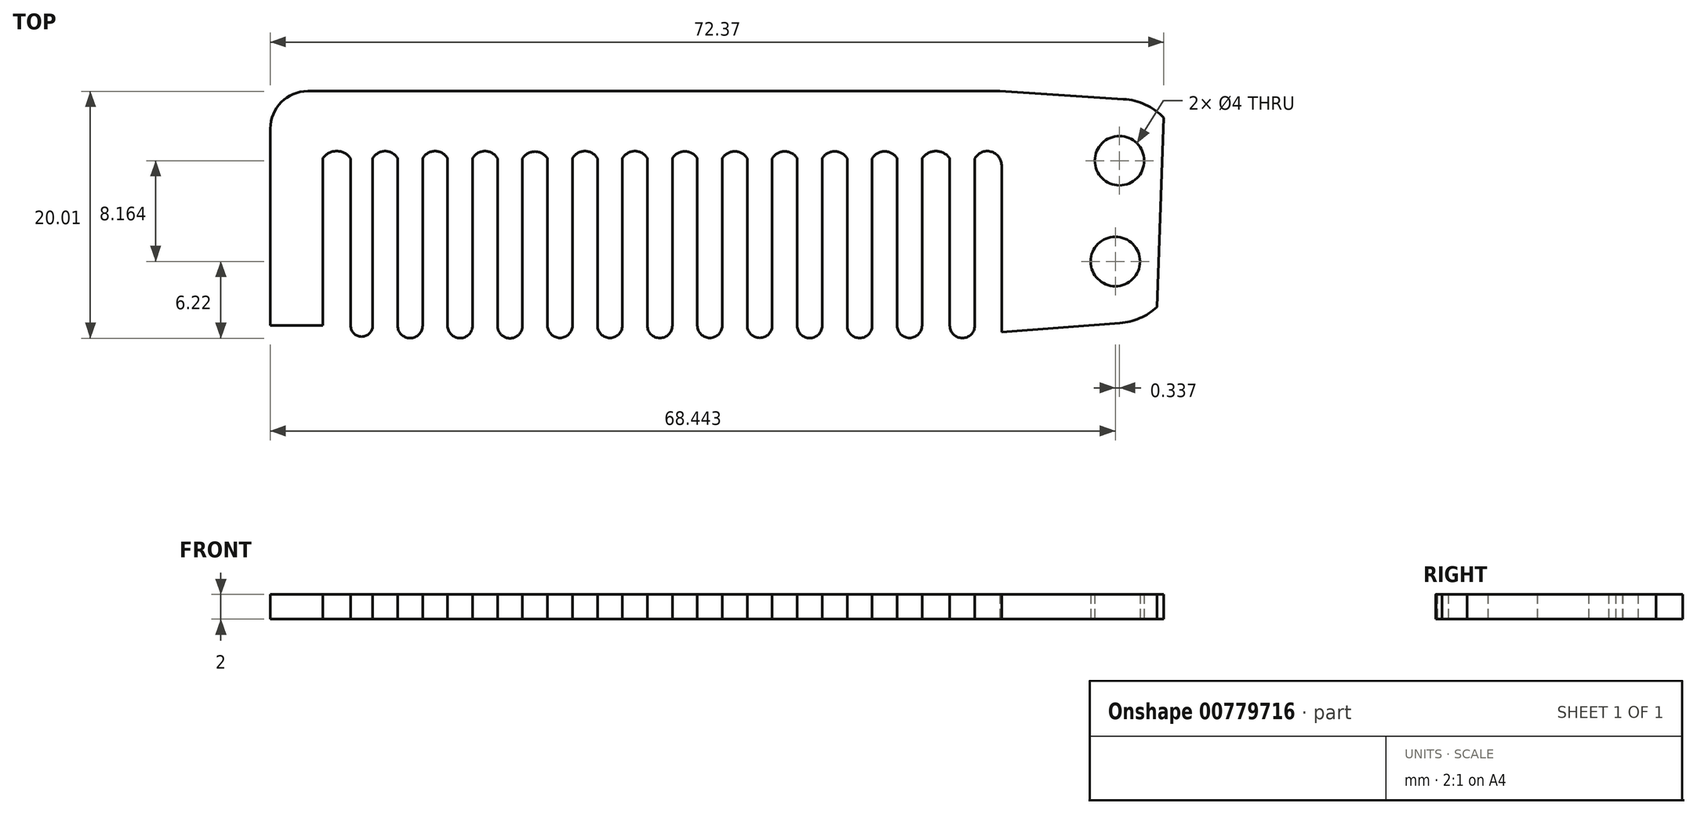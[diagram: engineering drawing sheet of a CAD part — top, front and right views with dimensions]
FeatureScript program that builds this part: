
annotation { "Feature Type Name" : "Feature", "Feature Type Description" : "" }
export const myFeature = defineFeature(function(context is Context, id is Id, definition is map)
    precondition{}
    {
        {
            var Q0;
            Q0=qCreatedBy(makeId("Top.planeOp"),FACE);
            var sketch = newSketch(context, id + "F0", { "sketchPlane" : qUnion([Q0])});
            skLineSegment(sketch, "E0", {"start": v(56.63, 10.5) * mm, "end": v(56.63, -3.03) * mm});
            skArc(sketch, "E1.filletArc", {"start": v(2.6, 15.95) * mm, "mid": v(0.46, 15.07) * mm, "end": v(-0.43, 12.92) * mm});
            skLineSegment(sketch, "E2", {"start": v(3.82, 2.37) * mm, "end": v(3.82, -3.03) * mm});
            skLineSegment(sketch, "E3", {"start": v(3.82, -3.03) * mm, "end": v(3.82, 10.5) * mm});
            skLineSegment(sketch, "E4", {"start": v(6.08, 2.37) * mm, "end": v(6.08, 10.5) * mm});
            skLineSegment(sketch, "E5", {"start": v(6.08, 10.5) * mm, "end": v(6.08, -3.03) * mm});
            skLineSegment(sketch, "E6", {"start": v(7.86, 2.37) * mm, "end": v(7.86, 10.5) * mm});
            skLineSegment(sketch, "E7", {"start": v(7.86, 10.5) * mm, "end": v(7.86, -3.03) * mm});
            skLineSegment(sketch, "E8", {"start": v(9.89, 2.37) * mm, "end": v(9.89, 10.5) * mm});
            skLineSegment(sketch, "E9", {"start": v(9.89, 10.5) * mm, "end": v(9.89, -3.03) * mm});
            skLineSegment(sketch, "E10", {"start": v(11.9, 2.37) * mm, "end": v(11.9, 10.5) * mm});
            skLineSegment(sketch, "E11", {"start": v(11.9, 10.5) * mm, "end": v(11.9, -3.03) * mm});
            skLineSegment(sketch, "E12", {"start": v(13.93, 2.37) * mm, "end": v(13.93, 10.5) * mm});
            skLineSegment(sketch, "E13", {"start": v(13.93, 10.5) * mm, "end": v(13.93, -3.03) * mm});
            skLineSegment(sketch, "E14", {"start": v(15.95, 2.37) * mm, "end": v(15.95, 10.5) * mm});
            skLineSegment(sketch, "E15", {"start": v(15.95, 10.5) * mm, "end": v(15.95, -3.03) * mm});
            skLineSegment(sketch, "E16", {"start": v(17.98, 10.5) * mm, "end": v(17.98, -3.06) * mm});
            skLineSegment(sketch, "E17", {"start": v(20, 2.37) * mm, "end": v(20, 10.5) * mm});
            skLineSegment(sketch, "E18", {"start": v(20, 10.5) * mm, "end": v(20, -3.06) * mm});
            skLineSegment(sketch, "E19", {"start": v(22.02, 2.37) * mm, "end": v(22.02, 10.5) * mm});
            skLineSegment(sketch, "E20", {"start": v(24.04, 2.37) * mm, "end": v(24.04, 10.5) * mm});
            skLineSegment(sketch, "E21", {"start": v(24.04, 2.37) * mm, "end": v(24.04, -3.03) * mm});
            skLineSegment(sketch, "E22", {"start": v(26.07, 2.37) * mm, "end": v(26.07, 10.5) * mm});
            skLineSegment(sketch, "E23", {"start": v(26.07, 10.5) * mm, "end": v(26.07, -3.03) * mm});
            skLineSegment(sketch, "E24", {"start": v(28.09, 2.37) * mm, "end": v(28.09, 10.5) * mm});
            skLineSegment(sketch, "E25", {"start": v(28.09, 2.37) * mm, "end": v(28.09, -3.03) * mm});
            skLineSegment(sketch, "E26", {"start": v(30.11, 2.37) * mm, "end": v(30.11, 10.5) * mm});
            skLineSegment(sketch, "E27", {"start": v(30.11, 10.5) * mm, "end": v(30.11, -3.03) * mm});
            skLineSegment(sketch, "E28", {"start": v(32.13, 2.37) * mm, "end": v(32.13, 10.5) * mm});
            skLineSegment(sketch, "E29", {"start": v(32.13, 10.5) * mm, "end": v(32.13, -3.03) * mm});
            skLineSegment(sketch, "E30", {"start": v(34.16, 2.37) * mm, "end": v(34.16, 10.5) * mm});
            skLineSegment(sketch, "E31", {"start": v(34.16, 10.5) * mm, "end": v(34.16, -3.03) * mm});
            skLineSegment(sketch, "E32", {"start": v(36.18, 2.37) * mm, "end": v(36.18, 10.5) * mm});
            skLineSegment(sketch, "E33", {"start": v(36.18, 10.5) * mm, "end": v(36.18, -3.03) * mm});
            skLineSegment(sketch, "E34", {"start": v(38.2, 2.37) * mm, "end": v(38.2, 10.5) * mm});
            skLineSegment(sketch, "E35", {"start": v(38.2, 10.5) * mm, "end": v(38.2, -3.03) * mm});
            skLineSegment(sketch, "E36", {"start": v(40.23, 2.37) * mm, "end": v(40.23, 10.5) * mm});
            skLineSegment(sketch, "E37", {"start": v(40.23, 10.5) * mm, "end": v(40.23, -3.03) * mm});
            skLineSegment(sketch, "E38", {"start": v(42.25, 2.37) * mm, "end": v(42.25, 10.5) * mm});
            skLineSegment(sketch, "E39", {"start": v(42.25, 10.5) * mm, "end": v(42.25, -3.03) * mm});
            skLineSegment(sketch, "E40", {"start": v(44.27, 2.37) * mm, "end": v(44.27, 10.5) * mm});
            skLineSegment(sketch, "E41", {"start": v(44.27, 10.5) * mm, "end": v(44.27, -3.03) * mm});
            skLineSegment(sketch, "E42", {"start": v(46.3, 2.37) * mm, "end": v(46.3, 10.5) * mm});
            skLineSegment(sketch, "E43", {"start": v(46.3, 10.5) * mm, "end": v(46.3, -3.03) * mm});
            skLineSegment(sketch, "E44", {"start": v(48.32, 2.37) * mm, "end": v(48.32, 10.5) * mm});
            skLineSegment(sketch, "E45", {"start": v(48.32, 10.5) * mm, "end": v(48.32, -3.03) * mm});
            skLineSegment(sketch, "E46", {"start": v(50.34, 2.37) * mm, "end": v(50.34, 10.5) * mm});
            skLineSegment(sketch, "E47", {"start": v(50.34, 10.5) * mm, "end": v(50.34, -3.03) * mm});
            skLineSegment(sketch, "E48", {"start": v(52.36, 2.37) * mm, "end": v(52.36, 10.5) * mm});
            skLineSegment(sketch, "E49", {"start": v(52.36, 10.5) * mm, "end": v(52.36, -3.03) * mm});
            skLineSegment(sketch, "E50", {"start": v(54.6, 2.37) * mm, "end": v(54.6, 10.5) * mm});
            skLineSegment(sketch, "E51", {"start": v(54.6, 10.5) * mm, "end": v(54.6, -3.03) * mm});
            skLineSegment(sketch, "E52", {"start": v(58.8, 9.96) * mm, "end": v(58.8, -3.3) * mm});
            skArc(sketch, "E53", {"start": v(9.89, -3.03) * mm, "mid": v(10.9, -4.05) * mm, "end": v(11.9, -3.03) * mm});
            skArc(sketch, "E54", {"start": v(13.93, -3.03) * mm, "mid": v(14.94, -4.05) * mm, "end": v(15.95, -3.03) * mm});
            skArc(sketch, "E55", {"start": v(17.98, -3.03) * mm, "mid": v(18.99, -4.06) * mm, "end": v(20, -3.03) * mm});
            skArc(sketch, "E56", {"start": v(22.02, -3.03) * mm, "mid": v(23.03, -4.03) * mm, "end": v(24.04, -3.03) * mm});
            skArc(sketch, "E57", {"start": v(26.07, -3.03) * mm, "mid": v(27.08, -4.03) * mm, "end": v(28.09, -3.03) * mm});
            skArc(sketch, "E58", {"start": v(30.11, -3.03) * mm, "mid": v(31.12, -4.04) * mm, "end": v(32.13, -3.03) * mm});
            skArc(sketch, "E59", {"start": v(34.16, -3.03) * mm, "mid": v(35.17, -4.03) * mm, "end": v(36.18, -3.03) * mm});
            skArc(sketch, "E60", {"start": v(38.2, -3.03) * mm, "mid": v(39.21, -4.02) * mm, "end": v(40.23, -3.03) * mm});
            skArc(sketch, "E61", {"start": v(42.25, -3.03) * mm, "mid": v(43.26, -4.05) * mm, "end": v(44.27, -3.03) * mm});
            skArc(sketch, "E62", {"start": v(46.3, -3.03) * mm, "mid": v(47.3, -4.04) * mm, "end": v(48.32, -3.03) * mm});
            skArc(sketch, "E63", {"start": v(50.34, -3.03) * mm, "mid": v(51.35, -4.03) * mm, "end": v(52.36, -3.03) * mm});
            skArc(sketch, "E64", {"start": v(54.6, -3.03) * mm, "mid": v(55.62, -4.04) * mm, "end": v(56.63, -3.03) * mm});
            skArc(sketch, "E65.filletArc", {"start": v(58.8, -3.3) * mm, "mid": v(58.8, -3.43) * mm, "end": v(58.81, -3.55) * mm});
            skArc(sketch, "E66", {"start": v(6.08, -3.03) * mm, "mid": v(6.97, -3.93) * mm, "end": v(7.86, -3.03) * mm});
            skArc(sketch, "E67", {"start": v(6.08, 10.5) * mm, "mid": v(4.95, 11.1) * mm, "end": v(3.82, 10.5) * mm});
            skArc(sketch, "E68", {"start": v(9.89, 10.5) * mm, "mid": v(8.87, 11.1) * mm, "end": v(7.86, 10.5) * mm});
            skArc(sketch, "E69", {"start": v(13.93, 10.5) * mm, "mid": v(12.92, 11.1) * mm, "end": v(11.9, 10.5) * mm});
            skArc(sketch, "E70", {"start": v(17.98, 10.5) * mm, "mid": v(16.97, 11.1) * mm, "end": v(15.95, 10.5) * mm});
            skArc(sketch, "E71", {"start": v(22.02, 10.5) * mm, "mid": v(21.01, 11.06) * mm, "end": v(20, 10.5) * mm});
            skArc(sketch, "E72", {"start": v(26.07, 10.5) * mm, "mid": v(25.06, 11.1) * mm, "end": v(24.04, 10.5) * mm});
            skArc(sketch, "E73", {"start": v(30.11, 10.5) * mm, "mid": v(29.1, 11.1) * mm, "end": v(28.09, 10.5) * mm});
            skArc(sketch, "E74", {"start": v(34.16, 10.5) * mm, "mid": v(33.15, 11.08) * mm, "end": v(32.13, 10.5) * mm});
            skArc(sketch, "E75", {"start": v(38.2, 10.5) * mm, "mid": v(37.2, 11.08) * mm, "end": v(36.18, 10.5) * mm});
            skArc(sketch, "E76", {"start": v(42.25, 10.5) * mm, "mid": v(41.24, 11.08) * mm, "end": v(40.23, 10.5) * mm});
            skArc(sketch, "E77", {"start": v(46.3, 10.5) * mm, "mid": v(45.28, 11.08) * mm, "end": v(44.27, 10.5) * mm});
            skArc(sketch, "E78", {"start": v(50.34, 10.5) * mm, "mid": v(49.33, 11.08) * mm, "end": v(48.32, 10.5) * mm});
            skArc(sketch, "E79", {"start": v(54.6, 10.5) * mm, "mid": v(53.49, 11.1) * mm, "end": v(52.36, 10.5) * mm});
            skArc(sketch, "E80", {"start": v(58.8, 9.96) * mm, "mid": v(57.93, 11.06) * mm, "end": v(56.63, 10.5) * mm});
            skLineSegment(sketch, "E81", {"start": v(22.02, 2.37) * mm, "end": v(22.02, -3.03) * mm});
            skLineSegment(sketch, "E82", {"start": v(78.8, 5.95) * mm, "end": v(78.8, 5.95) * mm});
            skLineSegment(sketch, "E83", {"start": v(2.6, 15.95) * mm, "end": v(58.65, 15.95) * mm});
            skPoint(sketch, "E84.visualSharp", {"position": v(78.8, -4.05) * mm});
            skPoint(sketch, "E85.visualSharp", {"position": v(78.8, 15.95) * mm});
            skPoint(sketch, "E86.visualSharp", {"position": v(78.8, 5.95) * mm});
            skCircle(sketch, "E87", {"center": v(68.01, 2.16) * mm, "radius": 2 * mm});
            skCircle(sketch, "E88", {"center": v(68.35, 10.32) * mm, "radius": 2 * mm});
            skLineSegment(sketch, "E89", {"start": v(58.65, 15.95) * mm, "end": v(68.67, 15.31) * mm});
            skLineSegment(sketch, "E90", {"start": v(58.81, -3.55) * mm, "end": v(68.4, -2.83) * mm});
            skPoint(sketch, "E91.visualSharp", {"position": v(70.4, 15.2) * mm});
            skArc(sketch, "E91.filletArc", {"start": v(71.94, 13.8) * mm, "mid": v(70.45, 14.86) * mm, "end": v(68.67, 15.31) * mm});
            skPoint(sketch, "E92.visualSharp", {"position": v(70.33, -2.68) * mm});
            skArc(sketch, "E92.filletArc", {"start": v(68.4, -2.83) * mm, "mid": v(70, -2.43) * mm, "end": v(71.39, -1.53) * mm});
            skLineSegment(sketch, "E93", {"start": v(-0.43, 12.92) * mm, "end": v(-0.43, -3.03) * mm});
            skLineSegment(sketch, "E94", {"start": v(-0.43, -3.03) * mm, "end": v(3.82, -3.03) * mm});
            skLineSegment(sketch, "E95", {"start": v(68.01, 2.16) * mm, "end": v(68.35, 10.32) * mm, "construction": true});
            skLineSegment(sketch, "E96", {"start": v(71.39, -1.53) * mm, "end": v(71.94, 13.8) * mm});
            skSolve(sketch);
        }
        {
            var Q0;
            Q0=qSketchRegion(id+"F0",true);
            var Q1;
            Q1=makeQuery(id+"F0.imprint","IMPRINT",FACE,{"disambiguationData":[TD([[makeQuery(id+"F0.imprint","IMPRINT",EDGE,{"derivedFrom":sQuery(id+"F0.wireOp",EDGE,"1oXmgVZ5-gnLq-iHea-oESG-ihjMs6EF8sqd")}),1.0]])]});
            var Q2;
            Q2=makeQuery(id+"F0.imprint","IMPRINT",FACE,{"disambiguationData":[TD([[makeQuery(id+"F0.imprint","IMPRINT",EDGE,{"derivedFrom":sQuery(id+"F0.wireOp",EDGE,"hkDLLBfR-qxi3-HcG5-FM2N-qt6i9bJRYM3o")}),1.0]])]});
            extrude(context, id + "F1", {"entities" : qUnion([Q0, Q1, Q2]), "depth" : 2 * mm, "offsetDistance" : 25 * mm});
        }
    });
